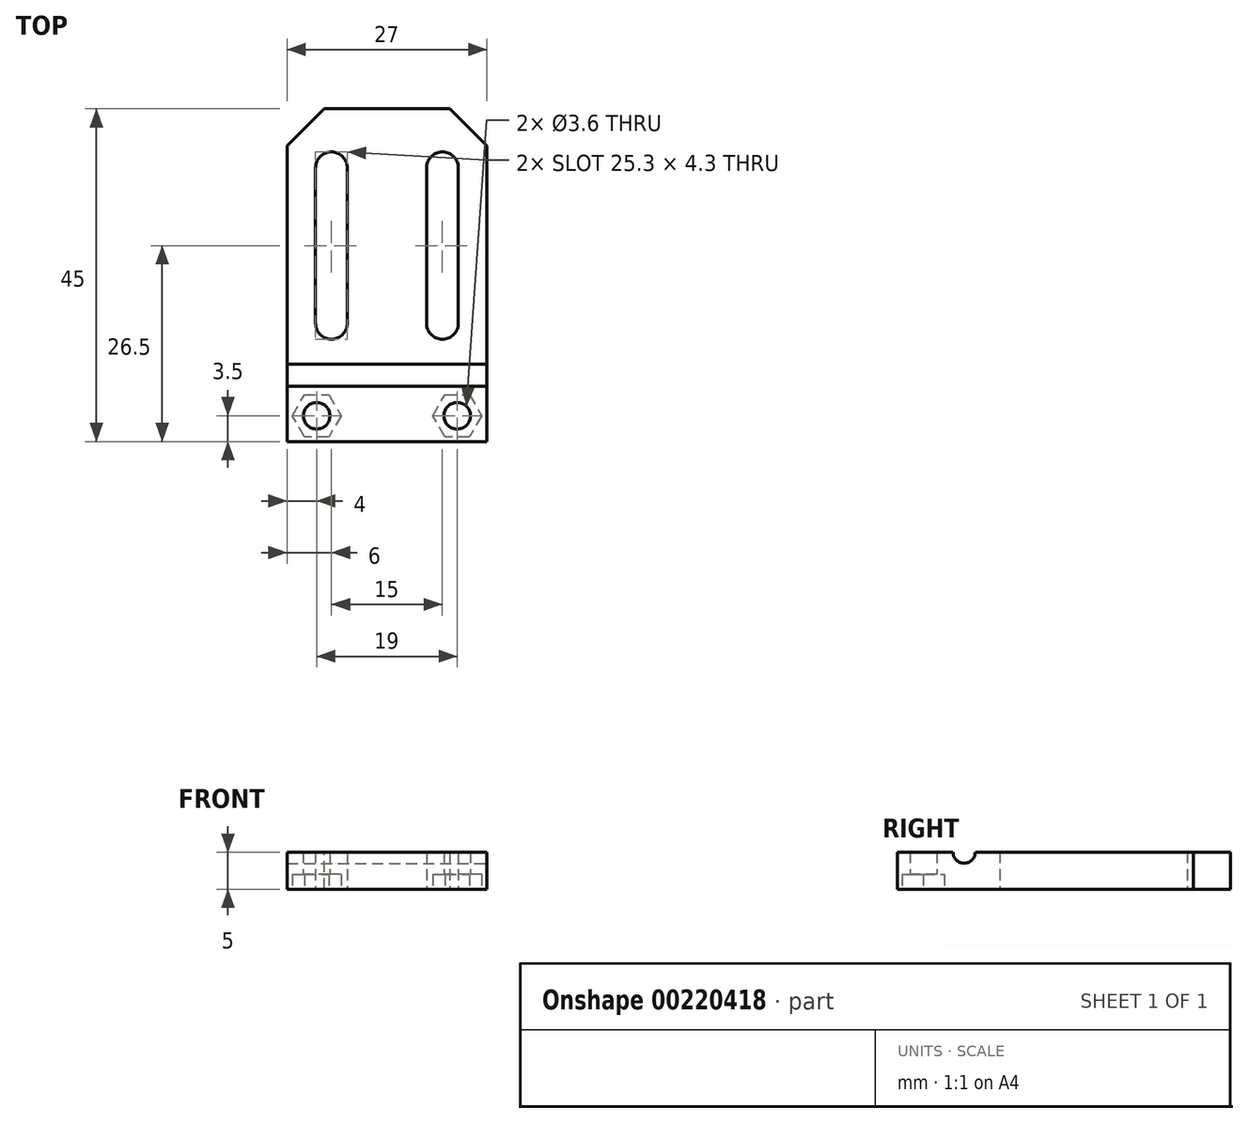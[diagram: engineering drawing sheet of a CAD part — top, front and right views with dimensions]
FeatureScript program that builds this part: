
annotation { "Feature Type Name" : "Feature", "Feature Type Description" : "" }
export const myFeature = defineFeature(function(context is Context, id is Id, definition is map)
    precondition{}
    {
        {
            var Q0;
            Q0=qCreatedBy(makeId("Top.planeOp"),FACE);
            var sketch = newSketch(context, id + "F0", { "sketchPlane" : qUnion([Q0])});
            skLineSegment(sketch, "E0.bottom", {"start": v(0, 0) * mm, "end": v(27, 0) * mm});
            skLineSegment(sketch, "E0.top", {"start": v(0, -45) * mm, "end": v(27, -45) * mm});
            skLineSegment(sketch, "E0.left", {"start": v(0, 0) * mm, "end": v(0, -45) * mm});
            skLineSegment(sketch, "E0.right", {"start": v(27, 0) * mm, "end": v(27, -45) * mm});
            skCircle(sketch, "E1", {"center": v(4, -41.5) * mm, "radius": 1.8 * mm});
            skCircle(sketch, "E2", {"center": v(23, -41.5) * mm, "radius": 1.8 * mm});
            skCircle(sketch, "E3", {"center": v(6, -8) * mm, "radius": 2.15 * mm, "construction": true});
            skCircle(sketch, "E4", {"center": v(21, -8) * mm, "radius": 2.15 * mm, "construction": true});
            skCircle(sketch, "E5", {"center": v(6, -29) * mm, "radius": 2.15 * mm, "construction": true});
            skCircle(sketch, "E6", {"center": v(21, -29) * mm, "radius": 2.15 * mm, "construction": true});
            skLineSegment(sketch, "E7", {"start": v(3.85, -8) * mm, "end": v(3.85, -29) * mm});
            skLineSegment(sketch, "E8", {"start": v(8.15, -8) * mm, "end": v(8.15, -29) * mm});
            skLineSegment(sketch, "E9", {"start": v(18.85, -8) * mm, "end": v(18.85, -29) * mm});
            skLineSegment(sketch, "E10", {"start": v(23.15, -8) * mm, "end": v(23.15, -29) * mm});
            skArc(sketch, "E11", {"start": v(3.85, -8) * mm, "mid": v(6, -5.85) * mm, "end": v(8.15, -8) * mm});
            skArc(sketch, "E12", {"start": v(18.85, -8) * mm, "mid": v(21, -5.85) * mm, "end": v(23.15, -8) * mm});
            skArc(sketch, "E13", {"start": v(23.15, -29) * mm, "mid": v(21, -31.15) * mm, "end": v(18.85, -29) * mm});
            skArc(sketch, "E14", {"start": v(8.15, -29) * mm, "mid": v(6, -31.15) * mm, "end": v(3.85, -29) * mm});
            skCircle(sketch, "E15.cCircle", {"center": v(4, -41.5) * mm, "radius": 2.85 * mm, "construction": true});
            skLineSegment(sketch, "E15.0", {"start": v(2.35, -38.65) * mm, "end": v(5.65, -38.65) * mm});
            skLineSegment(sketch, "E15.1", {"start": v(5.65, -38.65) * mm, "end": v(7.3, -41.5) * mm});
            skLineSegment(sketch, "E15.2", {"start": v(7.3, -41.5) * mm, "end": v(5.65, -44.35) * mm});
            skLineSegment(sketch, "E15.3", {"start": v(5.65, -44.35) * mm, "end": v(2.35, -44.35) * mm});
            skLineSegment(sketch, "E15.4", {"start": v(2.35, -44.35) * mm, "end": v(0.7, -41.5) * mm});
            skLineSegment(sketch, "E15.5", {"start": v(0.7, -41.5) * mm, "end": v(2.35, -38.65) * mm});
            skPoint(sketch, "E15.0.midPoint", {"position": v(4, -38.65) * mm});
            skCircle(sketch, "E16.cCircle", {"center": v(23, -41.5) * mm, "radius": 2.85 * mm, "construction": true});
            skLineSegment(sketch, "E16.0", {"start": v(21.35, -38.65) * mm, "end": v(24.65, -38.65) * mm});
            skLineSegment(sketch, "E16.1", {"start": v(24.65, -38.65) * mm, "end": v(26.3, -41.5) * mm});
            skLineSegment(sketch, "E16.2", {"start": v(26.3, -41.5) * mm, "end": v(24.65, -44.35) * mm});
            skLineSegment(sketch, "E16.3", {"start": v(24.65, -44.35) * mm, "end": v(21.35, -44.35) * mm});
            skLineSegment(sketch, "E16.4", {"start": v(21.35, -44.35) * mm, "end": v(19.7, -41.5) * mm});
            skLineSegment(sketch, "E16.5", {"start": v(19.7, -41.5) * mm, "end": v(21.35, -38.65) * mm});
            skPoint(sketch, "E16.0.midPoint", {"position": v(23, -38.65) * mm});
            skSolve(sketch);
        }
        {
            var Q0;
            Q0=makeQuery(id+"F0.imprint","IMPRINT",FACE,{"disambiguationData":[TD([[makeQuery(id+"F0.imprint","IMPRINT",EDGE,{"derivedFrom":sQuery(id+"F0.wireOp",EDGE,"E0.bottom")}),-1.0]])]});
            var Q1;
            Q1=makeQuery(id+"F0.imprint","IMPRINT",FACE,{"disambiguationData":[TD([[makeQuery(id+"F0.imprint","IMPRINT",EDGE,{"derivedFrom":sQuery(id+"F0.wireOp",EDGE,"E2")}),-1.0]])]});
            var Q2;
            Q2=makeQuery(id+"F0.imprint","IMPRINT",FACE,{"disambiguationData":[TD([[makeQuery(id+"F0.imprint","IMPRINT",EDGE,{"derivedFrom":sQuery(id+"F0.wireOp",EDGE,"E1")}),-1.0]])]});
            extrude(context, id + "F1", {"entities" : qUnion([Q0, Q1, Q2]), "depth" : 5 * mm});
        }
        {
            var Q0;
            Q0=makeQuery(id+"F1.opExtrude","SWEPT_FACE",FACE,{"disambiguationData":[OSD([sQuery(id+"F0.wireOp",EDGE,"E0.right")])]});
            var sketch = newSketch(context, id + "F2", { "sketchPlane" : qUnion([Q0])});
            skPoint(sketch, "E17.0", {"position": v(-41.5, 0) * mm});
            skLineSegment(sketch, "E18", {"start": v(-41.5, 0) * mm, "end": v(-41.5, 5) * mm, "construction": true});
            skArc(sketch, "E19", {"start": v(-37.5, 5) * mm, "mid": v(-36, 3.5) * mm, "end": v(-34.5, 5) * mm});
            skLineSegment(sketch, "E20", {"start": v(-45, 0) * mm, "end": v(-45, -1.5) * mm});
            skLineSegment(sketch, "E21", {"start": v(-45, -1.5) * mm, "end": v(-34.5, -1.5) * mm});
            skLineSegment(sketch, "E22", {"start": v(-34.5, -1.5) * mm, "end": v(-33, 0) * mm});
            skSolve(sketch);
        }
        {
            var Q0;
            Q0=qSketchRegion(id+"F2",true);
            var Q1;
            {var subQ0=sQuery(id+"F2.wireOp",EDGE,"E19");Q1=makeQuery(id+"F2.imprint","IMPRINT",FACE,{"disambiguationData":[TD([[makeQuery(id+"F2.imprint","IMPRINT",EDGE,{"derivedFrom":subQ0}),1.0]])]});}
            extrude(context, id + "F3", {"entities" : qUnion([Q0, Q1]), "operationType" : NewBodyOperationType.REMOVE, "endBound" : BoundingType.UP_TO_NEXT, "oppositeDirection" : true, "depth" : 25 * mm});
        }
        {
            var Q0;
            Q0=makeQuery(id+"F0.imprint","IMPRINT",FACE,{"disambiguationData":[TD([[makeQuery(id+"F0.imprint","IMPRINT",EDGE,{"derivedFrom":sQuery(id+"F0.wireOp",EDGE,"E1")}),1.0]])]});
            var Q1;
            Q1=makeQuery(id+"F0.imprint","IMPRINT",FACE,{"disambiguationData":[TD([[makeQuery(id+"F0.imprint","IMPRINT",EDGE,{"derivedFrom":sQuery(id+"F0.wireOp",EDGE,"E2")}),1.0]])]});
            var Q2;
            Q2=makeQuery(id+"F0.imprint","IMPRINT",FACE,{"disambiguationData":[TD([[makeQuery(id+"F0.imprint","IMPRINT",EDGE,{"derivedFrom":sQuery(id+"F0.wireOp",EDGE,"E1")}),-1.0]])]});
            var Q3;
            Q3=makeQuery(id+"F0.imprint","IMPRINT",FACE,{"disambiguationData":[TD([[makeQuery(id+"F0.imprint","IMPRINT",EDGE,{"derivedFrom":sQuery(id+"F0.wireOp",EDGE,"E2")}),-1.0]])]});
            extrude(context, id + "F4", {"entities" : qUnion([Q0, Q1, Q2, Q3]), "operationType" : NewBodyOperationType.REMOVE, "depth" : 2 * mm});
        }
        {
            var Q0;
            Q0=makeQuery(id+"F1.opExtrude","SWEPT_EDGE",EDGE,{"disambiguationData":[OSD([sQuery(id+"F0.wireOp",EDGE,"E0.bottom"),sQuery(id+"F0.wireOp",EDGE,"E0.left")])]});
            var Q1;
            Q1=makeQuery(id+"F1.opExtrude","SWEPT_EDGE",EDGE,{"disambiguationData":[OSD([sQuery(id+"F0.wireOp",EDGE,"E0.bottom"),sQuery(id+"F0.wireOp",EDGE,"E0.right")])]});
            chamfer(context, id + "F5", {"entities" : qUnion([Q0, Q1]), "width" : 5 * mm, "tangentPropagation" : true});
        }
    });
